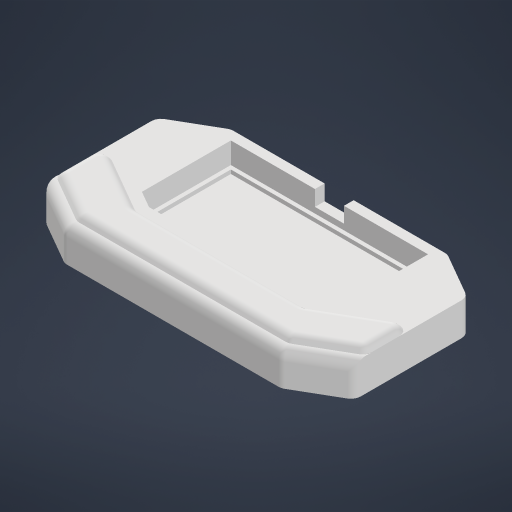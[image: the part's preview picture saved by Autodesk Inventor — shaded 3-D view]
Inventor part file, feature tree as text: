
AUTODESK INVENTOR PART (.ipt)
format: ipt  version: 2023.4 (Build 274418000, 418)  size: 435,200 bytes
history: native  units: mm
features: extrude x7, sketch x4, projected_geometry x4, fillet x3, other x3, chamfer x2, reference x1
ambient origin geometry x8: Origin, YZ Plane, XZ Plane, XY Plane, X Axis, Y Axis, Z Axis, Center Point
bodies: Solid1 (feature_tree)
feature tree (24):
  sketch  "Sketch1"  dims[d0=51.0mm d1=23.0mm]
  extrude  "Extrusion1"  Depth=23.0mm
  extrude  "Extrusion2"  Depth=2.5mm
  extrude  "Extrusion3"  Depth=1.0mm TaperAngle=0.0deg
  sketch  "Sketch2"  dims[d2=1.0mm d3=2.5mm]
  extrude  "Extrusion4"  Depth=7.5mm
  fillet  "Fillet1"  Radius=4.0mm
  extrude  "Extrusion5"  Depth=2.0mm
  chamfer  "Chamfer1"  Distance=15.0mm
  extrude  "Extrusion6"  TaperAngle=90.0deg  [1 undecoded]
  fillet  "Fillet2"  [1 undecoded]
  chamfer  "Chamfer2"  Angle=150.0deg  [1 undecoded]
  fillet  "Fillet3"  [1 undecoded]
  extrude  "Extrusion7"  Depth=2.5mm
  projected_geometry  "Projected Loop1"
  sketch  "Sketch3"  dims[d4=3.0mm d5=0.0mm d6=1.0mm d7=0.0mm]
  reference  "Reference1"
  projected_geometry  "Projected Loop2"
  projected_geometry  "Projected Loop3"
  sketch  "Sketch4"  dims[d8=5.5mm d9=0.0mm d10=7.5mm d11=4.0mm d12=0.0mm d13=15.0mm d20=15.0mm d21=90.0deg d22=60.0deg d23=150.0deg d24=150.0deg d25=2.5mm d26=3.0mm d27=0.0mm d28=1.675mm d29=2.0mm d30=45.0deg d31=0.25mm d32=1.25mm d33=0.0mm d34=2.5mm d35=1.25mm d36=2.0mm d37=45.0deg d38=2.5mm d40=40.0mm d41=49.8mm d42=49.8mm d43=7.85mm d44=3.0mm d45=3.0mm d46=3.75mm d47=4.2125mm d48=0.675mm d49=10.5mm d50=10.5mm d51=4.1mm d52=4.145mm d53=7.85mm d54=7.85mm d55=5.5mm d56=5.5mm d57=360.0deg d58=2.0mm d59=0.0mm d60=25.0mm]
  projected_geometry  "Projected Loop4"
  parser-record x1  (decoder bookkeeping rows leaked as tree rows — omitted from the tree; the rows remain in map.json)
  other  "Joystick Enclosure.iam"
  other  "Joystick Top:1"
note: 4 required parameter values undecoded (feature->parameter linkage not recoverable at this tier; creation-order binding heuristic only, values carry confidence <= 0.55)
note: 1 file-system path scrubbed to <path> (originals preserved in map.json)
